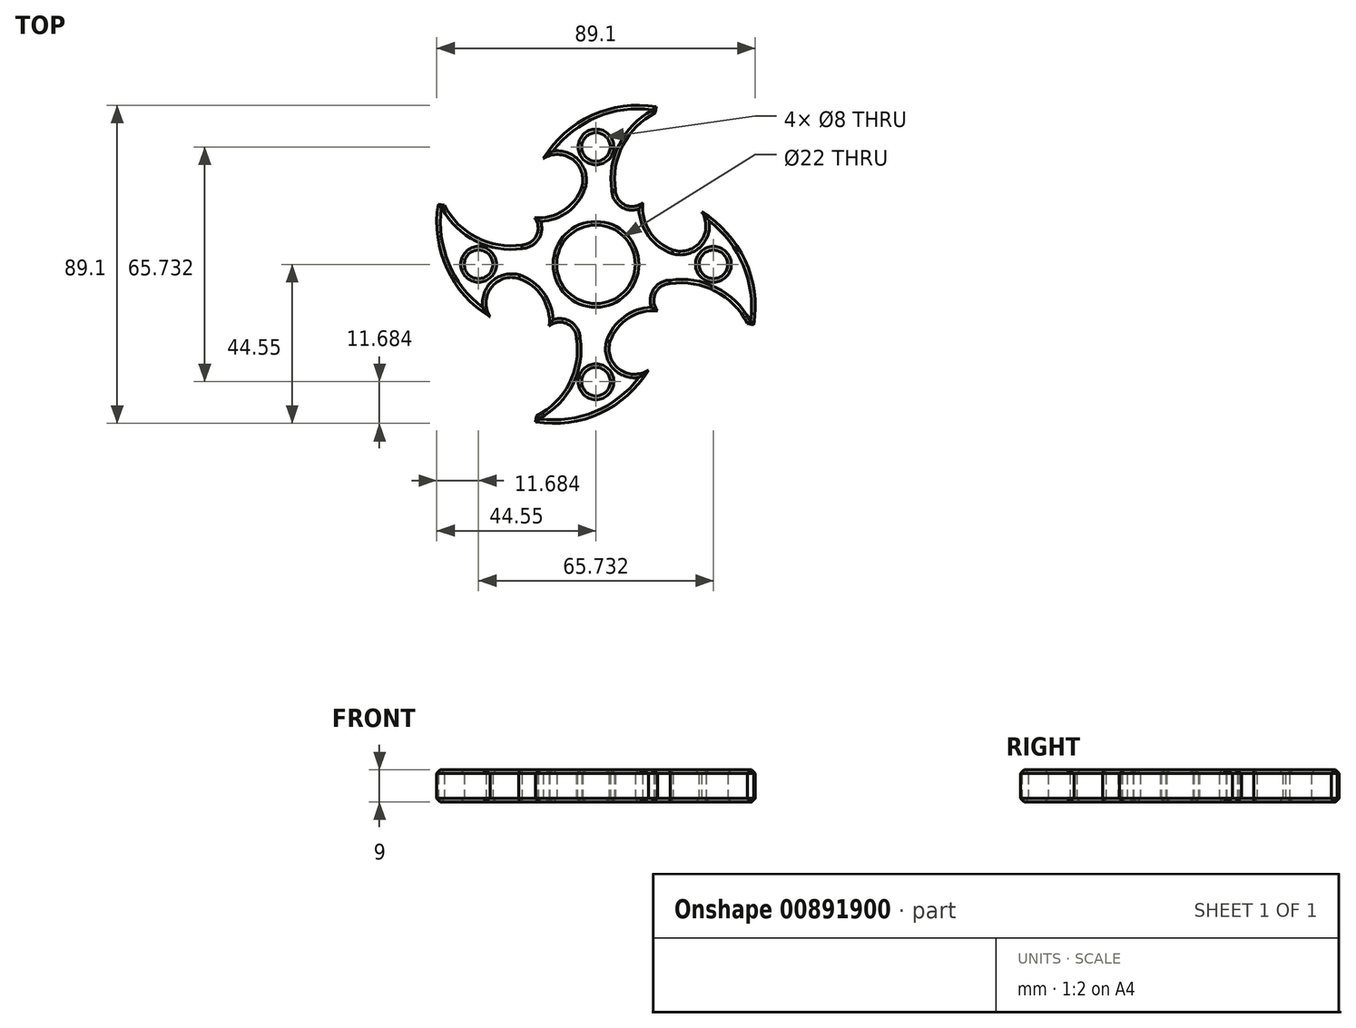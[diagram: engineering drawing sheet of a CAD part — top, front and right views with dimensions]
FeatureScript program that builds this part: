
annotation { "Feature Type Name" : "Feature", "Feature Type Description" : "" }
export const myFeature = defineFeature(function(context is Context, id is Id, definition is map)
    precondition{}
    {
        {
            var Q0;
            Q0=qCreatedBy(makeId("Top.planeOp"),FACE);
            var sketch = newSketch(context, id + "F0", { "sketchPlane" : qUnion([Q0])});
            skCircle(sketch, "E0", {"center": v(0, 0) * mm, "radius": 11 * mm});
            skArc(sketch, "E1", {"start": v(16.88, 44.14) * mm, "mid": v(-1.14, 41.7) * mm, "end": v(-14.7, 29.6) * mm});
            skArc(sketch, "E2", {"start": v(-3.97, 21.6) * mm, "mid": v(-6.54, 29.36) * mm, "end": v(-14.7, 29.6) * mm});
            skLineSegment(sketch, "E3", {"start": v(16.88, 44.14) * mm, "end": v(16.62, 42.44) * mm});
            skArc(sketch, "E4", {"start": v(-17.22, 13.05) * mm, "mid": v(-9.12, 15.05) * mm, "end": v(-3.97, 21.6) * mm});
            skArc(sketch, "E5.1.0", {"start": v(-44.14, 16.88) * mm, "mid": v(-41.7, -1.14) * mm, "end": v(-29.6, -14.7) * mm});
            skArc(sketch, "E5.1.2", {"start": v(-13.05, -17.22) * mm, "mid": v(-15.05, -9.12) * mm, "end": v(-21.6, -3.97) * mm});
            skArc(sketch, "E5.1.3", {"start": v(-21.6, -3.97) * mm, "mid": v(-29.36, -6.54) * mm, "end": v(-29.6, -14.7) * mm});
            skLineSegment(sketch, "E5.1.4", {"start": v(-44.14, 16.88) * mm, "end": v(-42.44, 16.62) * mm});
            skArc(sketch, "E5.2.0", {"start": v(-16.88, -44.14) * mm, "mid": v(1.14, -41.7) * mm, "end": v(14.7, -29.6) * mm});
            skArc(sketch, "E5.2.2", {"start": v(17.22, -13.05) * mm, "mid": v(9.12, -15.05) * mm, "end": v(3.97, -21.6) * mm});
            skArc(sketch, "E5.2.3", {"start": v(3.97, -21.6) * mm, "mid": v(6.54, -29.36) * mm, "end": v(14.7, -29.6) * mm});
            skLineSegment(sketch, "E5.2.4", {"start": v(-16.88, -44.14) * mm, "end": v(-16.62, -42.44) * mm});
            skArc(sketch, "E5.3.0", {"start": v(44.14, -16.88) * mm, "mid": v(41.7, 1.14) * mm, "end": v(29.6, 14.7) * mm});
            skArc(sketch, "E5.3.2", {"start": v(13.05, 17.22) * mm, "mid": v(15.05, 9.12) * mm, "end": v(21.6, 3.97) * mm});
            skArc(sketch, "E5.3.3", {"start": v(21.6, 3.97) * mm, "mid": v(29.36, 6.54) * mm, "end": v(29.6, 14.7) * mm});
            skLineSegment(sketch, "E5.3.4", {"start": v(44.14, -16.88) * mm, "end": v(42.44, -16.62) * mm});
            skCircle(sketch, "E6", {"center": v(0, 32.87) * mm, "radius": 4 * mm});
            skArc(sketch, "E7", {"start": v(16.62, 42.44) * mm, "mid": v(7.51, 33.4) * mm, "end": v(5.43, 20.76) * mm});
            skArc(sketch, "E8", {"start": v(5.43, 20.76) * mm, "mid": v(8.14, 16.62) * mm, "end": v(13.05, 17.22) * mm});
            skArc(sketch, "E9.1.0", {"start": v(-42.44, 16.62) * mm, "mid": v(-33.4, 7.51) * mm, "end": v(-20.76, 5.43) * mm});
            skArc(sketch, "E9.1.1", {"start": v(-20.76, 5.43) * mm, "mid": v(-16.62, 8.14) * mm, "end": v(-17.22, 13.05) * mm});
            skCircle(sketch, "E9.1.2", {"center": v(-32.87, 0) * mm, "radius": 4 * mm});
            skArc(sketch, "E9.2.0", {"start": v(-16.62, -42.44) * mm, "mid": v(-7.51, -33.4) * mm, "end": v(-5.43, -20.76) * mm});
            skArc(sketch, "E9.2.1", {"start": v(-5.43, -20.76) * mm, "mid": v(-8.14, -16.62) * mm, "end": v(-13.05, -17.22) * mm});
            skCircle(sketch, "E9.2.2", {"center": v(0, -32.87) * mm, "radius": 4 * mm});
            skArc(sketch, "E9.3.0", {"start": v(42.44, -16.62) * mm, "mid": v(33.4, -7.51) * mm, "end": v(20.76, -5.43) * mm});
            skArc(sketch, "E9.3.1", {"start": v(20.76, -5.43) * mm, "mid": v(16.62, -8.14) * mm, "end": v(17.22, -13.05) * mm});
            skCircle(sketch, "E9.3.2", {"center": v(32.87, 0) * mm, "radius": 4 * mm});
            skSolve(sketch);
        }
        {
            var Q0;
            Q0 = qSketchRegion(id + "F0", true);
            extrude(context, id + "F1", {"entities" : qUnion([Q0]), "depth" : 9 * mm, "offsetDistance" : 25 * mm});
        }
        {
            var Q0;
            Q0=makeQuery(id+"F1.opExtrude","CAP_FACE",FACE,{"disambiguationData":[OSD([sQuery(id+"F0.wireOp",EDGE,"E0"),sQuery(id+"F0.wireOp",EDGE,"E1"),sQuery(id+"F0.wireOp",EDGE,"E2"),sQuery(id+"F0.wireOp",EDGE,"E3"),sQuery(id+"F0.wireOp",EDGE,"E4"),sQuery(id+"F0.wireOp",EDGE,"E5.1.0"),sQuery(id+"F0.wireOp",EDGE,"E5.1.2"),sQuery(id+"F0.wireOp",EDGE,"E5.1.3"),sQuery(id+"F0.wireOp",EDGE,"E5.1.4"),sQuery(id+"F0.wireOp",EDGE,"E5.2.0"),sQuery(id+"F0.wireOp",EDGE,"E5.2.2"),sQuery(id+"F0.wireOp",EDGE,"E5.2.3"),sQuery(id+"F0.wireOp",EDGE,"E5.2.4"),sQuery(id+"F0.wireOp",EDGE,"E5.3.0"),sQuery(id+"F0.wireOp",EDGE,"E5.3.2"),sQuery(id+"F0.wireOp",EDGE,"E5.3.3"),sQuery(id+"F0.wireOp",EDGE,"E5.3.4"),sQuery(id+"F0.wireOp",EDGE,"E6"),sQuery(id+"F0.wireOp",EDGE,"E7"),sQuery(id+"F0.wireOp",EDGE,"E8"),sQuery(id+"F0.wireOp",EDGE,"E9.1.0"),sQuery(id+"F0.wireOp",EDGE,"E9.1.1"),sQuery(id+"F0.wireOp",EDGE,"E9.1.2"),sQuery(id+"F0.wireOp",EDGE,"E9.2.0"),sQuery(id+"F0.wireOp",EDGE,"E9.2.1"),sQuery(id+"F0.wireOp",EDGE,"E9.2.2"),sQuery(id+"F0.wireOp",EDGE,"E9.3.0"),sQuery(id+"F0.wireOp",EDGE,"E9.3.1"),sQuery(id+"F0.wireOp",EDGE,"E9.3.2")])],"isStart":false});
            var Q1;
            Q1=makeQuery(id+"F1.opExtrude","CAP_FACE",FACE,{"disambiguationData":[OSD([sQuery(id+"F0.wireOp",EDGE,"E0"),sQuery(id+"F0.wireOp",EDGE,"E1"),sQuery(id+"F0.wireOp",EDGE,"E2"),sQuery(id+"F0.wireOp",EDGE,"E3"),sQuery(id+"F0.wireOp",EDGE,"E4"),sQuery(id+"F0.wireOp",EDGE,"E5.1.0"),sQuery(id+"F0.wireOp",EDGE,"E5.1.2"),sQuery(id+"F0.wireOp",EDGE,"E5.1.3"),sQuery(id+"F0.wireOp",EDGE,"E5.1.4"),sQuery(id+"F0.wireOp",EDGE,"E5.2.0"),sQuery(id+"F0.wireOp",EDGE,"E5.2.2"),sQuery(id+"F0.wireOp",EDGE,"E5.2.3"),sQuery(id+"F0.wireOp",EDGE,"E5.2.4"),sQuery(id+"F0.wireOp",EDGE,"E5.3.0"),sQuery(id+"F0.wireOp",EDGE,"E5.3.2"),sQuery(id+"F0.wireOp",EDGE,"E5.3.3"),sQuery(id+"F0.wireOp",EDGE,"E5.3.4"),sQuery(id+"F0.wireOp",EDGE,"E6"),sQuery(id+"F0.wireOp",EDGE,"E7"),sQuery(id+"F0.wireOp",EDGE,"E8"),sQuery(id+"F0.wireOp",EDGE,"E9.1.0"),sQuery(id+"F0.wireOp",EDGE,"E9.1.1"),sQuery(id+"F0.wireOp",EDGE,"E9.1.2"),sQuery(id+"F0.wireOp",EDGE,"E9.2.0"),sQuery(id+"F0.wireOp",EDGE,"E9.2.1"),sQuery(id+"F0.wireOp",EDGE,"E9.2.2"),sQuery(id+"F0.wireOp",EDGE,"E9.3.0"),sQuery(id+"F0.wireOp",EDGE,"E9.3.1"),sQuery(id+"F0.wireOp",EDGE,"E9.3.2")])],"isStart":true});
            chamfer(context, id + "F2", {"entities" : qUnion([Q0, Q1]), "width" : 1 * mm, "tangentPropagation" : true});
        }
    });
